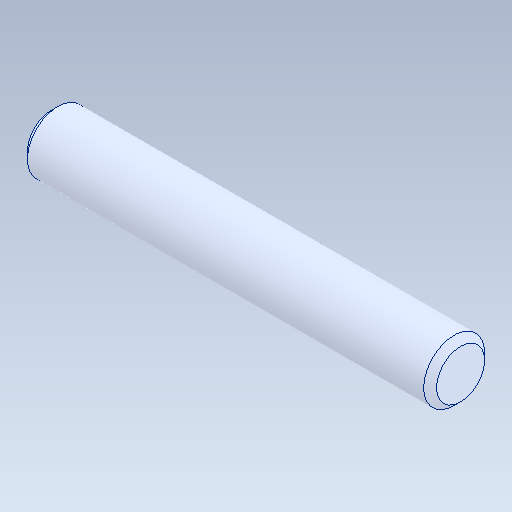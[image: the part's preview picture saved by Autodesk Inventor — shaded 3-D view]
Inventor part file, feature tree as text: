
AUTODESK INVENTOR PART (.ipt)
format: ipt  version: 2020 (Build 240168000, 168)  size: 91,136 bytes
history: native  units: in
note: dims shown in document units (in); Inventor stores cm internally (conversion verified against a paired STEP export)
features: chamfer x1
ambient origin geometry x8: Origin, YZ Plane, XZ Plane, XY Plane, X Axis, Y Axis, Z Axis, Center Point
bodies: Solid1 (feature_tree)
feature tree (1):
  chamfer  "Chamfer1"  [1 undecoded]
note: 1 required parameter value undecoded (feature->parameter linkage not recoverable at this tier; creation-order binding heuristic only, values carry confidence <= 0.55)
